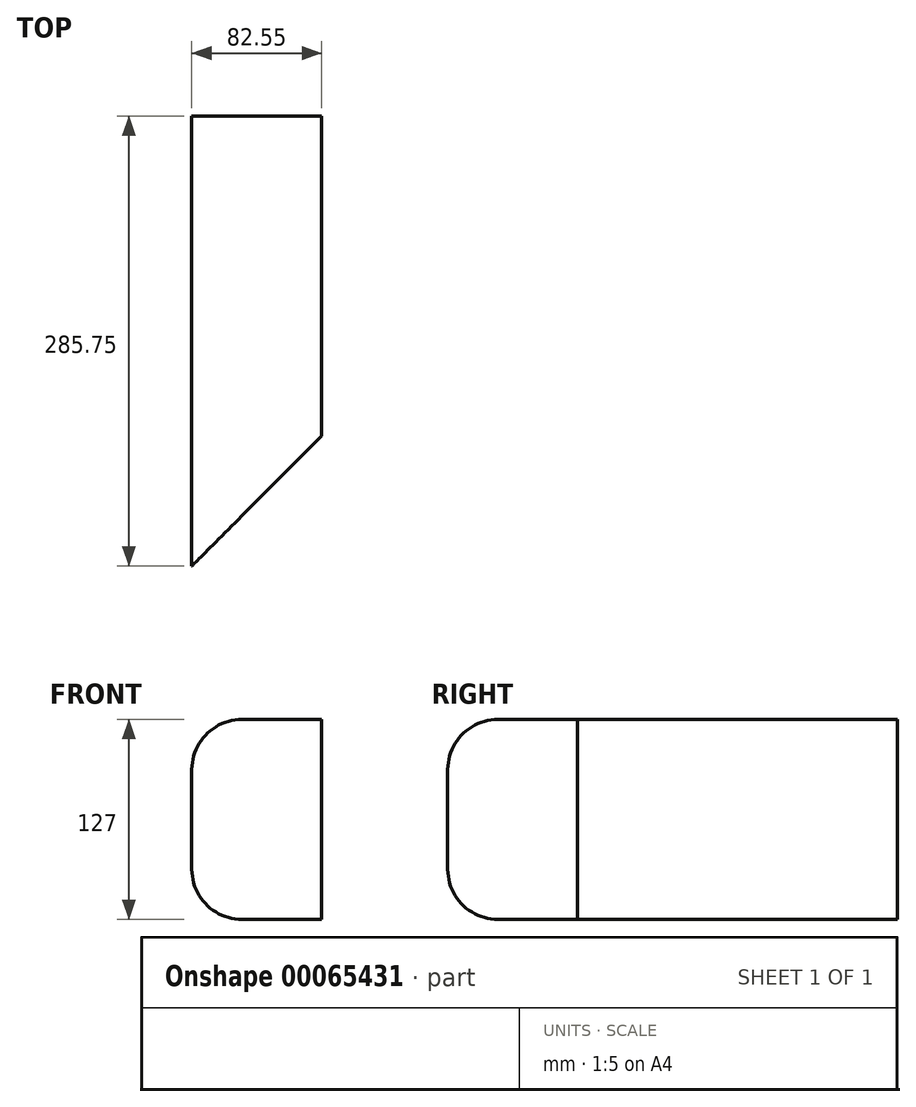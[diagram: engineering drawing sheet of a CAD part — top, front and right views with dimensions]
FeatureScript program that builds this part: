
annotation { "Feature Type Name" : "Feature", "Feature Type Description" : "" }
export const myFeature = defineFeature(function(context is Context, id is Id, definition is map)
    precondition{}
    {
        {
            var Q0;
            Q0=qCreatedBy(makeId("Front.planeOp"),FACE);
            var sketch = newSketch(context, id + "F0", { "sketchPlane" : qUnion([Q0])});
            skLineSegment(sketch, "E0.bottom", {"start": v(0, 0) * mm, "end": v(-50.8, 0) * mm});
            skLineSegment(sketch, "E0.top", {"start": v(0, -127) * mm, "end": v(-50.8, -127) * mm});
            skLineSegment(sketch, "E0.left", {"start": v(0, 0) * mm, "end": v(0, -127) * mm});
            skLineSegment(sketch, "E0.right", {"start": v(-82.55, -31.75) * mm, "end": v(-82.55, -95.25) * mm});
            skPoint(sketch, "E1.visualSharp", {"position": v(-82.55, 0) * mm});
            skArc(sketch, "E1.filletArc", {"start": v(-50.8, 0) * mm, "mid": v(-73.25, -9.3) * mm, "end": v(-82.55, -31.75) * mm});
            skPoint(sketch, "E2.visualSharp", {"position": v(-82.55, -127) * mm});
            skArc(sketch, "E2.filletArc", {"start": v(-82.55, -95.25) * mm, "mid": v(-73.25, -117.7) * mm, "end": v(-50.8, -127) * mm});
            skSolve(sketch);
        }
        {
            var Q0;
            Q0 = qSketchRegion(id + "F0", true);
            extrude(context, id + "F1", {"entities" : qUnion([Q0]), "depth" : 355.6 * mm});
        }
        {
            var Q0;
            Q0=makeQuery(id+"F1.opExtrude","SWEPT_FACE",FACE,{"disambiguationData":[OSD([sQuery(id+"F0.wireOp",EDGE,"E0.bottom")])]});
            var sketch = newSketch(context, id + "F2", { "sketchPlane" : qUnion([Q0])});
            skLineSegment(sketch, "E3", {"start": v(0, -203.2) * mm, "end": v(-152.4, -355.6) * mm});
            skLineSegment(sketch, "E4", {"start": v(0, -203.2) * mm, "end": v(0, -355.6) * mm});
            skLineSegment(sketch, "E5", {"start": v(0, -355.6) * mm, "end": v(-152.4, -355.6) * mm});
            skSolve(sketch);
        }
        {
            var Q0;
            Q0 = qSketchRegion(id + "F2", true);
            extrude(context, id + "F3", {"entities" : qUnion([Q0]), "operationType" : NewBodyOperationType.REMOVE, "endBound" : BoundingType.THROUGH_ALL, "oppositeDirection" : true, "depth" : 25.4 * mm});
        }
    });
